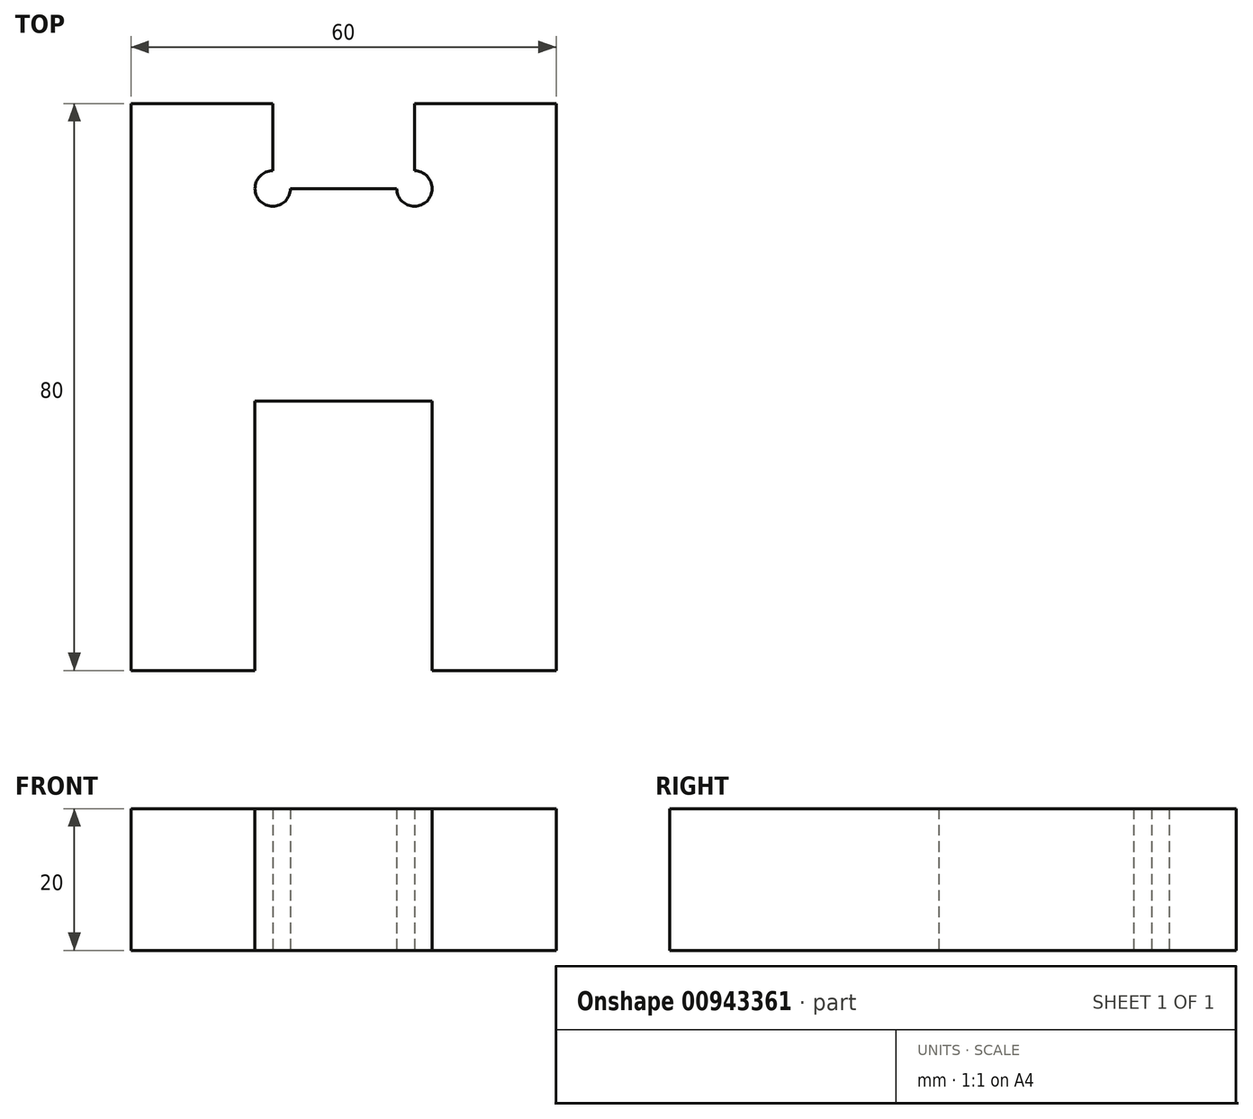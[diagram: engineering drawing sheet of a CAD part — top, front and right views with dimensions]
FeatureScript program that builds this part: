
annotation { "Feature Type Name" : "Feature", "Feature Type Description" : "" }
export const myFeature = defineFeature(function(context is Context, id is Id, definition is map)
    precondition{}
    {
        {
            var Q0;
            Q0=qCreatedBy(makeId("Top.planeOp"),FACE);
            var sketch = newSketch(context, id + "F0", { "sketchPlane" : qUnion([Q0])});
            skLineSegment(sketch, "E0.bottom", {"start": v(30, -40) * mm, "end": v(-30, -40) * mm});
            skLineSegment(sketch, "E0.top", {"start": v(30, 40) * mm, "end": v(10, 40) * mm});
            skLineSegment(sketch, "E0.left", {"start": v(30, -40) * mm, "end": v(30, 40) * mm});
            skLineSegment(sketch, "E0.right", {"start": v(-30, -40) * mm, "end": v(-30, 40) * mm});
            skPoint(sketch, "E0.middle", {"position": v(0, 0) * mm});
            skLineSegment(sketch, "E1", {"start": v(-10, 40) * mm, "end": v(-10, 30.5) * mm});
            skLineSegment(sketch, "E2", {"start": v(-7.5, 28) * mm, "end": v(7.5, 28) * mm});
            skLineSegment(sketch, "E3", {"start": v(10, 30.5) * mm, "end": v(10, 40) * mm});
            skLineSegment(sketch, "E4.trimOffspring", {"start": v(-10, 40) * mm, "end": v(-30, 40) * mm});
            skLineSegment(sketch, "E5", {"start": v(-12.5, -40) * mm, "end": v(-12.5, -2) * mm});
            skLineSegment(sketch, "E6", {"start": v(-12.5, -2) * mm, "end": v(12.5, -2) * mm});
            skLineSegment(sketch, "E7", {"start": v(12.5, -2) * mm, "end": v(12.5, -40) * mm});
            skArc(sketch, "E8", {"start": v(-10, 30.5) * mm, "mid": v(-11.77, 26.23) * mm, "end": v(-7.5, 28) * mm});
            skArc(sketch, "E9", {"start": v(7.5, 28) * mm, "mid": v(11.77, 26.23) * mm, "end": v(10, 30.5) * mm});
            skSolve(sketch);
        }
        {
            var Q0;
            Q0=makeQuery(id+"F0.imprint","IMPRINT",FACE,{"disambiguationData":[TD([[makeQuery(id+"F0.imprint","IMPRINT",EDGE,{"derivedFrom":sQuery(id+"F0.wireOp",EDGE,"E0.bottom")}),-1.0]])]});
            extrude(context, id + "F1", {"entities" : qUnion([Q0]), "depth" : 20 * mm, "offsetDistance" : 25 * mm});
        }
    });
